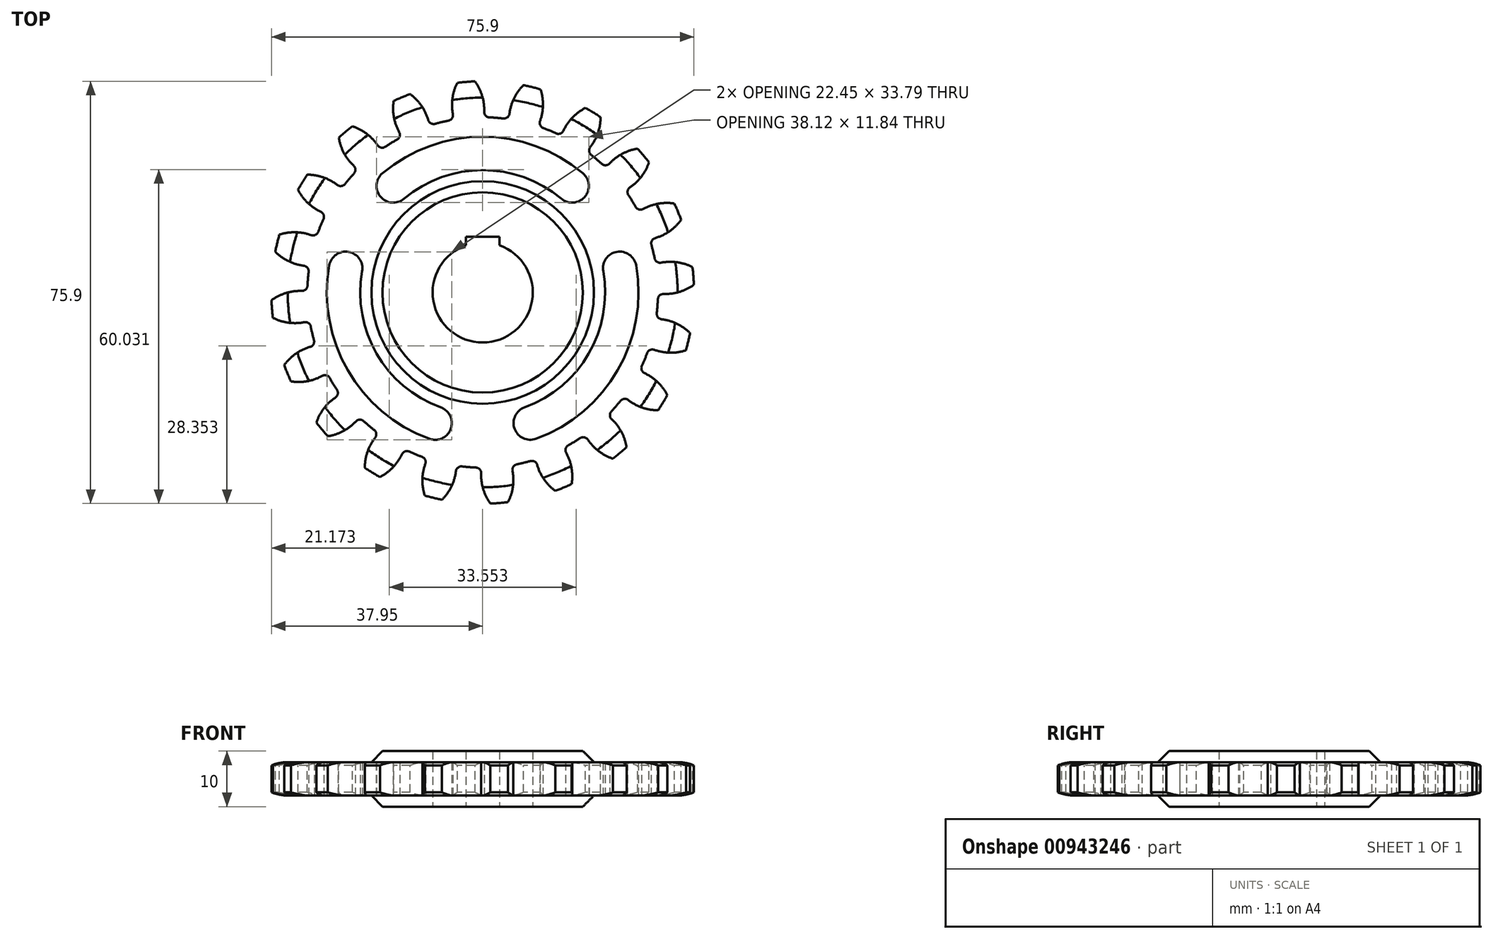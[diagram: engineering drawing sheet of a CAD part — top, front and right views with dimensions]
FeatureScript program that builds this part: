
annotation { "Feature Type Name" : "Feature", "Feature Type Description" : "" }
export const myFeature = defineFeature(function(context is Context, id is Id, definition is map)
    precondition{}
    {
        {
            var Q0;
            Q0=qCreatedBy(makeId("Top.planeOp"),FACE);
            var sketch = newSketch(context, id + "F0", { "sketchPlane" : qUnion([Q0])});
            skArc(sketch, "E0", {"start": v(-3, 8.49) * mm, "mid": v(0, -9) * mm, "end": v(3, 8.49) * mm});
            skCircle(sketch, "E1", {"center": v(0, 0) * mm, "radius": 25 * mm, "construction": true});
            skPoint(sketch, "E2", {"position": v(-46.68, 29.9) * mm});
            skArc(sketch, "E3", {"start": v(-21.67, 3.82) * mm, "mid": v(-24.1, 7.3) * mm, "end": v(-27.57, 4.86) * mm});
            skLineSegment(sketch, "E4", {"start": v(0, 0) * mm, "end": v(-24.62, 4.34) * mm, "construction": true});
            skArc(sketch, "E5", {"start": v(-9.58, -26.31) * mm, "mid": v(-5.73, -24.52) * mm, "end": v(-7.52, -20.67) * mm});
            skLineSegment(sketch, "E6", {"start": v(-8.55, -23.5) * mm, "end": v(0, 0) * mm, "construction": true});
            skArc(sketch, "E7", {"start": v(-27.57, 4.86) * mm, "mid": v(-24.25, -14) * mm, "end": v(-9.58, -26.31) * mm});
            skArc(sketch, "E8", {"start": v(-21.67, 3.82) * mm, "mid": v(-19.05, -11) * mm, "end": v(-7.52, -20.67) * mm});
            skArc(sketch, "E9.1.0", {"start": v(7.52, -20.67) * mm, "mid": v(19.05, -11) * mm, "end": v(21.67, 3.82) * mm});
            skArc(sketch, "E9.1.1", {"start": v(7.52, -20.67) * mm, "mid": v(5.73, -24.52) * mm, "end": v(9.58, -26.31) * mm});
            skArc(sketch, "E9.1.2", {"start": v(9.58, -26.31) * mm, "mid": v(24.25, -14) * mm, "end": v(27.57, 4.86) * mm});
            skArc(sketch, "E9.1.3", {"start": v(27.57, 4.86) * mm, "mid": v(24.1, 7.3) * mm, "end": v(21.67, 3.82) * mm});
            skArc(sketch, "E9.2.0", {"start": v(14.14, 16.85) * mm, "mid": v(0, 22) * mm, "end": v(-14.14, 16.85) * mm});
            skArc(sketch, "E9.2.1", {"start": v(14.14, 16.85) * mm, "mid": v(18.37, 17.22) * mm, "end": v(18, 21.45) * mm});
            skArc(sketch, "E9.2.2", {"start": v(18, 21.45) * mm, "mid": v(0, 28) * mm, "end": v(-18, 21.45) * mm});
            skLineSegment(sketch, "E10", {"start": v(-3, 8.49) * mm, "end": v(-3, 10) * mm});
            skLineSegment(sketch, "E11", {"start": v(-3, 10) * mm, "end": v(3, 10) * mm});
            skLineSegment(sketch, "E12", {"start": v(3, 10) * mm, "end": v(3, 8.49) * mm});
            skArc(sketch, "E13", {"start": v(-18, 21.45) * mm, "mid": v(-18.37, 17.22) * mm, "end": v(-14.14, 16.85) * mm});
            skArc(sketch, "E14", {"start": v(-1.4, 37.97) * mm, "mid": v(-2.98, 37.88) * mm, "end": v(-4.55, 37.73) * mm});
            skArc(sketch, "E15", {"start": v(-28.6, 13.2) * mm, "mid": v(-29.1, 12.05) * mm, "end": v(-29.55, 10.9) * mm});
            skLineSegment(sketch, "E16", {"start": v(0, 0) * mm, "end": v(0, 47.52) * mm, "construction": true});
            skArc(sketch, "E17", {"start": v(0.27, 32.5) * mm, "mid": v(-0.1, 35.38) * mm, "end": v(-1.4, 37.97) * mm});
            skLineSegment(sketch, "E18", {"start": v(0, 0) * mm, "end": v(-2.98, 37.88) * mm, "construction": true});
            skArc(sketch, "E19.MirrorCS", {"start": v(-5.36, 32.07) * mm, "mid": v(-5.43, 34.96) * mm, "end": v(-4.55, 37.73) * mm});
            skArc(sketch, "E20", {"start": v(-5.48, 34.57) * mm, "mid": v(2.75, -34.9) * mm, "end": v(0, 35) * mm, "construction": true});
            skArc(sketch, "E21", {"start": v(0, 35) * mm, "mid": v(-2.75, 34.9) * mm, "end": v(-5.48, 34.57) * mm, "construction": true});
            skArc(sketch, "E22", {"start": v(-6.14, 30.9) * mm, "mid": v(-5.5, 31.32) * mm, "end": v(-5.36, 32.07) * mm});
            skPoint(sketch, "E23.orphan", {"position": v(-5.1, 31.08) * mm});
            skArc(sketch, "E24.MirrorCS", {"start": v(1.23, 31.48) * mm, "mid": v(0.54, 31.8) * mm, "end": v(0.27, 32.5) * mm});
            skPoint(sketch, "E25.orphan", {"position": v(0.18, 31.5) * mm});
            skArc(sketch, "E26.1.0", {"start": v(3.7, 31.28) * mm, "mid": v(4.44, 31.49) * mm, "end": v(4.82, 32.15) * mm});
            skArc(sketch, "E26.1.1", {"start": v(4.82, 32.15) * mm, "mid": v(5.64, 34.93) * mm, "end": v(7.33, 37.29) * mm});
            skArc(sketch, "E26.1.2", {"start": v(10.4, 36.55) * mm, "mid": v(8.87, 36.95) * mm, "end": v(7.33, 37.29) * mm});
            skArc(sketch, "E26.1.3", {"start": v(10.3, 30.83) * mm, "mid": v(10.83, 33.68) * mm, "end": v(10.4, 36.55) * mm});
            skArc(sketch, "E26.1.4", {"start": v(10.9, 29.55) * mm, "mid": v(10.34, 30.07) * mm, "end": v(10.3, 30.83) * mm});
            skArc(sketch, "E26.2.0", {"start": v(13.2, 28.6) * mm, "mid": v(13.95, 28.57) * mm, "end": v(14.51, 29.1) * mm});
            skArc(sketch, "E26.2.1", {"start": v(14.51, 29.1) * mm, "mid": v(16.16, 31.48) * mm, "end": v(18.5, 33.2) * mm});
            skArc(sketch, "E26.2.2", {"start": v(21.18, 31.55) * mm, "mid": v(19.86, 32.4) * mm, "end": v(18.5, 33.2) * mm});
            skArc(sketch, "E26.2.3", {"start": v(19.33, 26.14) * mm, "mid": v(20.7, 28.69) * mm, "end": v(21.18, 31.55) * mm});
            skArc(sketch, "E26.2.4", {"start": v(19.5, 24.74) * mm, "mid": v(19.13, 25.4) * mm, "end": v(19.33, 26.14) * mm});
            skArc(sketch, "E26.3.0", {"start": v(21.38, 23.13) * mm, "mid": v(22.1, 22.86) * mm, "end": v(22.8, 23.18) * mm});
            skArc(sketch, "E26.3.1", {"start": v(22.8, 23.18) * mm, "mid": v(25.1, 24.94) * mm, "end": v(27.85, 25.86) * mm});
            skArc(sketch, "E26.3.2", {"start": v(29.9, 23.46) * mm, "mid": v(28.9, 24.68) * mm, "end": v(27.85, 25.86) * mm});
            skArc(sketch, "E26.3.3", {"start": v(26.46, 18.89) * mm, "mid": v(28.56, 20.89) * mm, "end": v(29.9, 23.46) * mm});
            skArc(sketch, "E26.3.4", {"start": v(26.19, 17.5) * mm, "mid": v(26.04, 18.25) * mm, "end": v(26.46, 18.89) * mm});
            skArc(sketch, "E26.4.0", {"start": v(27.48, 15.39) * mm, "mid": v(28.08, 14.92) * mm, "end": v(28.84, 15) * mm});
            skArc(sketch, "E26.4.1", {"start": v(28.84, 15) * mm, "mid": v(31.58, 15.97) * mm, "end": v(34.47, 15.98) * mm});
            skArc(sketch, "E26.4.2", {"start": v(35.68, 13.07) * mm, "mid": v(35.1, 14.54) * mm, "end": v(34.47, 15.98) * mm});
            skArc(sketch, "E26.4.3", {"start": v(31, 9.79) * mm, "mid": v(33.62, 11.04) * mm, "end": v(35.68, 13.07) * mm});
            skArc(sketch, "E26.4.4", {"start": v(30.32, 8.55) * mm, "mid": v(30.4, 9.31) * mm, "end": v(31, 9.79) * mm});
            skArc(sketch, "E26.5.0", {"start": v(30.9, 6.14) * mm, "mid": v(31.32, 5.5) * mm, "end": v(32.07, 5.36) * mm});
            skArc(sketch, "E26.5.1", {"start": v(32.07, 5.36) * mm, "mid": v(34.96, 5.43) * mm, "end": v(37.73, 4.55) * mm});
            skArc(sketch, "E26.5.2", {"start": v(37.97, 1.4) * mm, "mid": v(37.88, 2.98) * mm, "end": v(37.73, 4.55) * mm});
            skArc(sketch, "E26.5.3", {"start": v(32.5, -0.27) * mm, "mid": v(35.38, 0.1) * mm, "end": v(37.97, 1.4) * mm});
            skArc(sketch, "E26.5.4", {"start": v(31.48, -1.23) * mm, "mid": v(31.8, -0.54) * mm, "end": v(32.5, -0.27) * mm});
            skArc(sketch, "E26.6.0", {"start": v(31.28, -3.7) * mm, "mid": v(31.49, -4.44) * mm, "end": v(32.15, -4.82) * mm});
            skArc(sketch, "E26.6.1", {"start": v(32.15, -4.82) * mm, "mid": v(34.93, -5.64) * mm, "end": v(37.29, -7.33) * mm});
            skArc(sketch, "E26.6.2", {"start": v(36.55, -10.4) * mm, "mid": v(36.95, -8.87) * mm, "end": v(37.29, -7.33) * mm});
            skArc(sketch, "E26.6.3", {"start": v(30.83, -10.3) * mm, "mid": v(33.68, -10.83) * mm, "end": v(36.55, -10.4) * mm});
            skArc(sketch, "E26.6.4", {"start": v(29.55, -10.9) * mm, "mid": v(30.07, -10.34) * mm, "end": v(30.83, -10.3) * mm});
            skArc(sketch, "E26.7.0", {"start": v(28.6, -13.2) * mm, "mid": v(28.57, -13.95) * mm, "end": v(29.1, -14.51) * mm});
            skArc(sketch, "E26.7.1", {"start": v(29.1, -14.51) * mm, "mid": v(31.48, -16.16) * mm, "end": v(33.2, -18.5) * mm});
            skArc(sketch, "E26.7.2", {"start": v(31.55, -21.18) * mm, "mid": v(32.4, -19.86) * mm, "end": v(33.2, -18.5) * mm});
            skArc(sketch, "E26.7.3", {"start": v(26.14, -19.33) * mm, "mid": v(28.69, -20.7) * mm, "end": v(31.55, -21.18) * mm});
            skArc(sketch, "E26.7.4", {"start": v(24.74, -19.5) * mm, "mid": v(25.4, -19.13) * mm, "end": v(26.14, -19.33) * mm});
            skArc(sketch, "E26.8.0", {"start": v(23.13, -21.38) * mm, "mid": v(22.86, -22.1) * mm, "end": v(23.18, -22.8) * mm});
            skArc(sketch, "E26.8.1", {"start": v(23.18, -22.8) * mm, "mid": v(24.94, -25.1) * mm, "end": v(25.86, -27.85) * mm});
            skArc(sketch, "E26.8.2", {"start": v(23.46, -29.9) * mm, "mid": v(24.68, -28.9) * mm, "end": v(25.86, -27.85) * mm});
            skArc(sketch, "E26.8.3", {"start": v(18.89, -26.46) * mm, "mid": v(20.89, -28.56) * mm, "end": v(23.46, -29.9) * mm});
            skArc(sketch, "E26.8.4", {"start": v(17.5, -26.19) * mm, "mid": v(18.25, -26.04) * mm, "end": v(18.89, -26.46) * mm});
            skArc(sketch, "E26.9.0", {"start": v(15.39, -27.48) * mm, "mid": v(14.92, -28.08) * mm, "end": v(15, -28.84) * mm});
            skArc(sketch, "E26.9.1", {"start": v(15, -28.84) * mm, "mid": v(15.97, -31.58) * mm, "end": v(15.98, -34.47) * mm});
            skArc(sketch, "E26.9.2", {"start": v(13.07, -35.68) * mm, "mid": v(14.54, -35.1) * mm, "end": v(15.98, -34.47) * mm});
            skArc(sketch, "E26.9.3", {"start": v(9.79, -31) * mm, "mid": v(11.04, -33.62) * mm, "end": v(13.07, -35.68) * mm});
            skArc(sketch, "E26.9.4", {"start": v(8.55, -30.32) * mm, "mid": v(9.31, -30.4) * mm, "end": v(9.79, -31) * mm});
            skArc(sketch, "E26.10.0", {"start": v(6.14, -30.9) * mm, "mid": v(5.5, -31.32) * mm, "end": v(5.36, -32.07) * mm});
            skArc(sketch, "E26.10.1", {"start": v(5.36, -32.07) * mm, "mid": v(5.43, -34.96) * mm, "end": v(4.55, -37.73) * mm});
            skArc(sketch, "E26.10.2", {"start": v(1.4, -37.97) * mm, "mid": v(2.98, -37.88) * mm, "end": v(4.55, -37.73) * mm});
            skArc(sketch, "E26.10.3", {"start": v(-0.27, -32.5) * mm, "mid": v(0.1, -35.38) * mm, "end": v(1.4, -37.97) * mm});
            skArc(sketch, "E26.10.4", {"start": v(-1.23, -31.48) * mm, "mid": v(-0.54, -31.8) * mm, "end": v(-0.27, -32.5) * mm});
            skArc(sketch, "E26.11.0", {"start": v(-3.7, -31.28) * mm, "mid": v(-4.44, -31.49) * mm, "end": v(-4.82, -32.15) * mm});
            skArc(sketch, "E26.11.1", {"start": v(-4.82, -32.15) * mm, "mid": v(-5.64, -34.93) * mm, "end": v(-7.33, -37.29) * mm});
            skArc(sketch, "E26.11.2", {"start": v(-10.4, -36.55) * mm, "mid": v(-8.87, -36.95) * mm, "end": v(-7.33, -37.29) * mm});
            skArc(sketch, "E26.11.3", {"start": v(-10.3, -30.83) * mm, "mid": v(-10.83, -33.68) * mm, "end": v(-10.4, -36.55) * mm});
            skArc(sketch, "E26.11.4", {"start": v(-10.9, -29.55) * mm, "mid": v(-10.34, -30.07) * mm, "end": v(-10.3, -30.83) * mm});
            skArc(sketch, "E26.12.0", {"start": v(-13.2, -28.6) * mm, "mid": v(-13.95, -28.57) * mm, "end": v(-14.51, -29.1) * mm});
            skArc(sketch, "E26.12.1", {"start": v(-14.51, -29.1) * mm, "mid": v(-16.16, -31.48) * mm, "end": v(-18.5, -33.2) * mm});
            skArc(sketch, "E26.12.2", {"start": v(-21.18, -31.55) * mm, "mid": v(-19.86, -32.4) * mm, "end": v(-18.5, -33.2) * mm});
            skArc(sketch, "E26.12.3", {"start": v(-19.33, -26.14) * mm, "mid": v(-20.7, -28.69) * mm, "end": v(-21.18, -31.55) * mm});
            skArc(sketch, "E26.12.4", {"start": v(-19.5, -24.74) * mm, "mid": v(-19.13, -25.4) * mm, "end": v(-19.33, -26.14) * mm});
            skArc(sketch, "E26.13.0", {"start": v(-21.38, -23.13) * mm, "mid": v(-22.1, -22.86) * mm, "end": v(-22.8, -23.18) * mm});
            skArc(sketch, "E26.13.1", {"start": v(-22.8, -23.18) * mm, "mid": v(-25.1, -24.94) * mm, "end": v(-27.85, -25.86) * mm});
            skArc(sketch, "E26.13.2", {"start": v(-29.9, -23.46) * mm, "mid": v(-28.9, -24.68) * mm, "end": v(-27.85, -25.86) * mm});
            skArc(sketch, "E26.13.3", {"start": v(-26.46, -18.89) * mm, "mid": v(-28.56, -20.89) * mm, "end": v(-29.9, -23.46) * mm});
            skArc(sketch, "E26.13.4", {"start": v(-26.19, -17.5) * mm, "mid": v(-26.04, -18.25) * mm, "end": v(-26.46, -18.89) * mm});
            skArc(sketch, "E26.14.0", {"start": v(-27.48, -15.39) * mm, "mid": v(-28.08, -14.92) * mm, "end": v(-28.84, -15) * mm});
            skArc(sketch, "E26.14.1", {"start": v(-28.84, -15) * mm, "mid": v(-31.58, -15.97) * mm, "end": v(-34.47, -15.98) * mm});
            skArc(sketch, "E26.14.2", {"start": v(-35.68, -13.07) * mm, "mid": v(-35.1, -14.54) * mm, "end": v(-34.47, -15.98) * mm});
            skArc(sketch, "E26.14.3", {"start": v(-31, -9.79) * mm, "mid": v(-33.62, -11.04) * mm, "end": v(-35.68, -13.07) * mm});
            skArc(sketch, "E26.14.4", {"start": v(-30.32, -8.55) * mm, "mid": v(-30.4, -9.31) * mm, "end": v(-31, -9.79) * mm});
            skArc(sketch, "E26.15.0", {"start": v(-30.9, -6.14) * mm, "mid": v(-31.32, -5.5) * mm, "end": v(-32.07, -5.36) * mm});
            skArc(sketch, "E26.15.1", {"start": v(-32.07, -5.36) * mm, "mid": v(-34.96, -5.43) * mm, "end": v(-37.73, -4.55) * mm});
            skArc(sketch, "E26.15.2", {"start": v(-37.97, -1.4) * mm, "mid": v(-37.88, -2.98) * mm, "end": v(-37.73, -4.55) * mm});
            skArc(sketch, "E26.15.3", {"start": v(-32.5, 0.27) * mm, "mid": v(-35.38, -0.1) * mm, "end": v(-37.97, -1.4) * mm});
            skArc(sketch, "E26.15.4", {"start": v(-31.48, 1.23) * mm, "mid": v(-31.8, 0.54) * mm, "end": v(-32.5, 0.27) * mm});
            skArc(sketch, "E26.16.0", {"start": v(-31.28, 3.7) * mm, "mid": v(-31.49, 4.44) * mm, "end": v(-32.15, 4.82) * mm});
            skArc(sketch, "E26.16.1", {"start": v(-32.15, 4.82) * mm, "mid": v(-34.93, 5.64) * mm, "end": v(-37.29, 7.33) * mm});
            skArc(sketch, "E26.16.2", {"start": v(-36.55, 10.4) * mm, "mid": v(-36.95, 8.87) * mm, "end": v(-37.29, 7.33) * mm});
            skArc(sketch, "E26.16.3", {"start": v(-30.83, 10.3) * mm, "mid": v(-33.68, 10.83) * mm, "end": v(-36.55, 10.4) * mm});
            skArc(sketch, "E26.16.4", {"start": v(-29.55, 10.9) * mm, "mid": v(-30.07, 10.34) * mm, "end": v(-30.83, 10.3) * mm});
            skArc(sketch, "E26.17.0", {"start": v(-28.6, 13.2) * mm, "mid": v(-28.57, 13.95) * mm, "end": v(-29.1, 14.51) * mm});
            skArc(sketch, "E26.17.1", {"start": v(-29.1, 14.51) * mm, "mid": v(-31.48, 16.16) * mm, "end": v(-33.2, 18.5) * mm});
            skArc(sketch, "E26.17.2", {"start": v(-31.55, 21.18) * mm, "mid": v(-32.4, 19.86) * mm, "end": v(-33.2, 18.5) * mm});
            skArc(sketch, "E26.17.3", {"start": v(-26.14, 19.33) * mm, "mid": v(-28.69, 20.7) * mm, "end": v(-31.55, 21.18) * mm});
            skArc(sketch, "E26.17.4", {"start": v(-24.74, 19.5) * mm, "mid": v(-25.4, 19.13) * mm, "end": v(-26.14, 19.33) * mm});
            skArc(sketch, "E26.18.0", {"start": v(-23.13, 21.38) * mm, "mid": v(-22.86, 22.1) * mm, "end": v(-23.18, 22.8) * mm});
            skArc(sketch, "E26.18.1", {"start": v(-23.18, 22.8) * mm, "mid": v(-24.94, 25.1) * mm, "end": v(-25.86, 27.85) * mm});
            skArc(sketch, "E26.18.2", {"start": v(-23.46, 29.9) * mm, "mid": v(-24.68, 28.9) * mm, "end": v(-25.86, 27.85) * mm});
            skArc(sketch, "E26.18.3", {"start": v(-18.89, 26.46) * mm, "mid": v(-20.89, 28.56) * mm, "end": v(-23.46, 29.9) * mm});
            skArc(sketch, "E26.18.4", {"start": v(-17.5, 26.19) * mm, "mid": v(-18.25, 26.04) * mm, "end": v(-18.89, 26.46) * mm});
            skArc(sketch, "E26.19.0", {"start": v(-15.39, 27.48) * mm, "mid": v(-14.92, 28.08) * mm, "end": v(-15, 28.84) * mm});
            skArc(sketch, "E26.19.1", {"start": v(-15, 28.84) * mm, "mid": v(-15.97, 31.58) * mm, "end": v(-15.98, 34.47) * mm});
            skArc(sketch, "E26.19.2", {"start": v(-13.07, 35.68) * mm, "mid": v(-14.54, 35.1) * mm, "end": v(-15.98, 34.47) * mm});
            skArc(sketch, "E26.19.3", {"start": v(-9.79, 31) * mm, "mid": v(-11.04, 33.62) * mm, "end": v(-13.07, 35.68) * mm});
            skArc(sketch, "E26.19.4", {"start": v(-8.55, 30.32) * mm, "mid": v(-9.31, 30.4) * mm, "end": v(-9.79, 31) * mm});
            skLineSegment(sketch, "E26.anchor1", {"start": v(0, 0) * mm, "end": v(-6.14, 30.9) * mm, "construction": true});
            skLineSegment(sketch, "E26.anchor2", {"start": v(0, 0) * mm, "end": v(-15.39, 27.48) * mm, "construction": true});
            skArc(sketch, "E27.trimOffspring", {"start": v(-23.13, 21.38) * mm, "mid": v(-23.95, 20.46) * mm, "end": v(-24.74, 19.5) * mm});
            skArc(sketch, "E28.trimOffspring", {"start": v(-15.39, 27.48) * mm, "mid": v(-16.46, 26.86) * mm, "end": v(-17.5, 26.19) * mm});
            skArc(sketch, "E29.trimOffspring", {"start": v(-6.14, 30.9) * mm, "mid": v(-7.35, 30.63) * mm, "end": v(-8.55, 30.32) * mm});
            skArc(sketch, "E30.trimOffspring", {"start": v(3.7, 31.28) * mm, "mid": v(2.47, 31.4) * mm, "end": v(1.23, 31.48) * mm});
            skArc(sketch, "E31.trimOffspring", {"start": v(13.2, 28.6) * mm, "mid": v(12.05, 29.1) * mm, "end": v(10.9, 29.55) * mm});
            skArc(sketch, "E32.trimOffspring", {"start": v(21.38, 23.13) * mm, "mid": v(20.46, 23.95) * mm, "end": v(19.5, 24.74) * mm});
            skArc(sketch, "E33.trimOffspring", {"start": v(27.48, 15.39) * mm, "mid": v(26.86, 16.46) * mm, "end": v(26.19, 17.5) * mm});
            skArc(sketch, "E34.trimOffspring", {"start": v(30.9, 6.14) * mm, "mid": v(30.63, 7.35) * mm, "end": v(30.32, 8.55) * mm});
            skArc(sketch, "E35.trimOffspring", {"start": v(31.28, -3.7) * mm, "mid": v(31.4, -2.47) * mm, "end": v(31.48, -1.23) * mm});
            skArc(sketch, "E36.trimOffspring", {"start": v(28.6, -13.2) * mm, "mid": v(29.1, -12.05) * mm, "end": v(29.55, -10.9) * mm});
            skArc(sketch, "E37.trimOffspring", {"start": v(23.13, -21.38) * mm, "mid": v(23.95, -20.46) * mm, "end": v(24.74, -19.5) * mm});
            skArc(sketch, "E38.trimOffspring", {"start": v(15.39, -27.48) * mm, "mid": v(16.46, -26.86) * mm, "end": v(17.5, -26.19) * mm});
            skArc(sketch, "E39.trimOffspring", {"start": v(6.14, -30.9) * mm, "mid": v(7.35, -30.63) * mm, "end": v(8.55, -30.32) * mm});
            skArc(sketch, "E40.trimOffspring", {"start": v(-3.7, -31.28) * mm, "mid": v(-2.47, -31.4) * mm, "end": v(-1.23, -31.48) * mm});
            skArc(sketch, "E41.trimOffspring", {"start": v(-13.2, -28.6) * mm, "mid": v(-12.05, -29.1) * mm, "end": v(-10.9, -29.55) * mm});
            skArc(sketch, "E42.trimOffspring", {"start": v(-21.38, -23.13) * mm, "mid": v(-20.46, -23.95) * mm, "end": v(-19.5, -24.74) * mm});
            skArc(sketch, "E43.trimOffspring", {"start": v(-27.48, -15.39) * mm, "mid": v(-26.86, -16.46) * mm, "end": v(-26.19, -17.5) * mm});
            skArc(sketch, "E44.trimOffspring", {"start": v(-30.9, -6.14) * mm, "mid": v(-30.63, -7.35) * mm, "end": v(-30.32, -8.55) * mm});
            skArc(sketch, "E45.trimOffspring", {"start": v(-31.28, 3.7) * mm, "mid": v(-31.4, 2.47) * mm, "end": v(-31.48, 1.23) * mm});
            skSolve(sketch);
        }
        {
            var Q0;
            Q0=makeQuery(id+"F0.imprint","IMPRINT",FACE,{"disambiguationData":[TD([[makeQuery(id+"F0.imprint","IMPRINT",EDGE,{"derivedFrom":sQuery(id+"F0.wireOp",EDGE,"E0")}),-1.0]])]});
            extrude(context, id + "F1", {"entities" : qUnion([Q0]), "endBound" : BoundingType.SYMMETRIC, "depth" : 6 * mm, "offsetDistance" : 25 * mm});
        }
        {
            var Q0;
            Q0=qCreatedBy(makeId("Right.planeOp"),FACE);
            var sketch = newSketch(context, id + "F2", { "sketchPlane" : qUnion([Q0])});
            skLineSegment(sketch, "E46", {"start": v(37.97, 2.44) * mm, "end": v(37.97, -2.43) * mm});
            skLineSegment(sketch, "E47", {"start": v(34.73, 3) * mm, "end": v(34.73, -9.64) * mm, "construction": true});
            skArc(sketch, "E48", {"start": v(37.97, 2.44) * mm, "mid": v(36.38, 2.87) * mm, "end": v(34.73, 3) * mm});
            skArc(sketch, "E49.MirrorCS", {"start": v(37.97, -2.44) * mm, "mid": v(36.38, -2.87) * mm, "end": v(34.73, -3) * mm});
            skLineSegment(sketch, "E50", {"start": v(34.73, 3) * mm, "end": v(34.73, 3.33) * mm});
            skLineSegment(sketch, "E51", {"start": v(34.73, 3.33) * mm, "end": v(39.08, 3.33) * mm});
            skLineSegment(sketch, "E52", {"start": v(39.08, 3.33) * mm, "end": v(39.08, -3.22) * mm});
            skLineSegment(sketch, "E53", {"start": v(39.08, -3.22) * mm, "end": v(34.73, -3.32) * mm});
            skLineSegment(sketch, "E54", {"start": v(34.73, -3.32) * mm, "end": v(34.73, -3) * mm});
            skSolve(sketch);
        }
        {
            var Q0;
            Q0=makeQuery(id+"F2.imprint","IMPRINT",FACE,{"disambiguationData":[TD([[makeQuery(id+"F2.imprint","IMPRINT",EDGE,{"derivedFrom":sQuery(id+"F2.wireOp",EDGE,"E46")}),1.0]])]});
            var Q1;
            Q1=makeQuery(id+"F1.opExtrude","SWEPT_FACE",FACE,{"disambiguationData":[OSD([sQuery(id+"F0.wireOp",EDGE,"E0")])]});
            revolve(context, id + "F3", {"operationType" : NewBodyOperationType.REMOVE, "surfaceOperationType" : NewSurfaceOperationType.NEW, "entities" : qUnion([Q0]), "axis" : qUnion([Q1]), "revolveType" : RevolveType.FULL, "oppositeDirection" : true});
        }
        {
            var Q0;
            Q0=qCreatedBy(makeId("Top.planeOp"),FACE);
            var sketch = newSketch(context, id + "F4", { "sketchPlane" : qUnion([Q0])});
            skCircle(sketch, "E55", {"center": v(0, 0) * mm, "radius": 18 * mm});
            skArc(sketch, "E56", {"start": v(-3, 8.49) * mm, "mid": v(0, -9) * mm, "end": v(3, 8.49) * mm});
            skLineSegment(sketch, "E57", {"start": v(3, 8.49) * mm, "end": v(3, 10) * mm});
            skLineSegment(sketch, "E58", {"start": v(3, 10) * mm, "end": v(-3, 10) * mm});
            skLineSegment(sketch, "E59", {"start": v(-3, 10) * mm, "end": v(-3, 8.49) * mm});
            skSolve(sketch);
        }
        {
            var Q0;
            Q0=qSketchRegion(id+"F4",true);
            extrude(context, id + "F5", {"entities" : qUnion([Q0]), "operationType" : NewBodyOperationType.ADD, "endBound" : BoundingType.SYMMETRIC, "depth" : 10 * mm, "offsetDistance" : 25 * mm});
        }
        {
            var Q0;
            Q0=makeQuery(id+"F5.boolean.opBoolean","INTERSECT",EDGE,{"derivedFrom":[makeQuery(id+"F1.opExtrude","CAP_FACE",FACE,{"disambiguationData":[OSD([sQuery(id+"F0.wireOp",EDGE,"E0"),sQuery(id+"F0.wireOp",EDGE,"E3"),sQuery(id+"F0.wireOp",EDGE,"E5"),sQuery(id+"F0.wireOp",EDGE,"E7"),sQuery(id+"F0.wireOp",EDGE,"E8"),sQuery(id+"F0.wireOp",EDGE,"E9.1.0"),sQuery(id+"F0.wireOp",EDGE,"E9.1.1"),sQuery(id+"F0.wireOp",EDGE,"E9.1.2"),sQuery(id+"F0.wireOp",EDGE,"E9.1.3"),sQuery(id+"F0.wireOp",EDGE,"E9.2.0"),sQuery(id+"F0.wireOp",EDGE,"E9.2.1"),sQuery(id+"F0.wireOp",EDGE,"E9.2.2"),sQuery(id+"F0.wireOp",EDGE,"E10"),sQuery(id+"F0.wireOp",EDGE,"E11"),sQuery(id+"F0.wireOp",EDGE,"E12"),sQuery(id+"F0.wireOp",EDGE,"E13"),sQuery(id+"F0.wireOp",EDGE,"E14"),sQuery(id+"F0.wireOp",EDGE,"E15"),sQuery(id+"F0.wireOp",EDGE,"E17"),sQuery(id+"F0.wireOp",EDGE,"E19.MirrorCS"),sQuery(id+"F0.wireOp",EDGE,"E22"),sQuery(id+"F0.wireOp",EDGE,"E24.MirrorCS"),sQuery(id+"F0.wireOp",EDGE,"E26.1.0"),sQuery(id+"F0.wireOp",EDGE,"E26.1.1"),sQuery(id+"F0.wireOp",EDGE,"E26.1.2"),sQuery(id+"F0.wireOp",EDGE,"E26.1.3"),sQuery(id+"F0.wireOp",EDGE,"E26.1.4"),sQuery(id+"F0.wireOp",EDGE,"E26.2.0"),sQuery(id+"F0.wireOp",EDGE,"E26.2.1"),sQuery(id+"F0.wireOp",EDGE,"E26.2.2"),sQuery(id+"F0.wireOp",EDGE,"E26.2.3"),sQuery(id+"F0.wireOp",EDGE,"E26.2.4"),sQuery(id+"F0.wireOp",EDGE,"E26.3.0"),sQuery(id+"F0.wireOp",EDGE,"E26.3.1"),sQuery(id+"F0.wireOp",EDGE,"E26.3.2"),sQuery(id+"F0.wireOp",EDGE,"E26.3.3"),sQuery(id+"F0.wireOp",EDGE,"E26.3.4"),sQuery(id+"F0.wireOp",EDGE,"E26.4.0"),sQuery(id+"F0.wireOp",EDGE,"E26.4.1"),sQuery(id+"F0.wireOp",EDGE,"E26.4.2"),sQuery(id+"F0.wireOp",EDGE,"E26.4.3"),sQuery(id+"F0.wireOp",EDGE,"E26.4.4"),sQuery(id+"F0.wireOp",EDGE,"E26.5.0"),sQuery(id+"F0.wireOp",EDGE,"E26.5.1"),sQuery(id+"F0.wireOp",EDGE,"E26.5.2"),sQuery(id+"F0.wireOp",EDGE,"E26.5.3"),sQuery(id+"F0.wireOp",EDGE,"E26.5.4"),sQuery(id+"F0.wireOp",EDGE,"E26.6.0"),sQuery(id+"F0.wireOp",EDGE,"E26.6.1"),sQuery(id+"F0.wireOp",EDGE,"E26.6.2"),sQuery(id+"F0.wireOp",EDGE,"E26.6.3"),sQuery(id+"F0.wireOp",EDGE,"E26.6.4"),sQuery(id+"F0.wireOp",EDGE,"E26.7.0"),sQuery(id+"F0.wireOp",EDGE,"E26.7.1"),sQuery(id+"F0.wireOp",EDGE,"E26.7.2"),sQuery(id+"F0.wireOp",EDGE,"E26.7.3"),sQuery(id+"F0.wireOp",EDGE,"E26.7.4"),sQuery(id+"F0.wireOp",EDGE,"E26.8.0"),sQuery(id+"F0.wireOp",EDGE,"E26.8.1"),sQuery(id+"F0.wireOp",EDGE,"E26.8.2"),sQuery(id+"F0.wireOp",EDGE,"E26.8.3"),sQuery(id+"F0.wireOp",EDGE,"E26.8.4"),sQuery(id+"F0.wireOp",EDGE,"E26.9.0"),sQuery(id+"F0.wireOp",EDGE,"E26.9.1"),sQuery(id+"F0.wireOp",EDGE,"E26.9.2"),sQuery(id+"F0.wireOp",EDGE,"E26.9.3"),sQuery(id+"F0.wireOp",EDGE,"E26.9.4"),sQuery(id+"F0.wireOp",EDGE,"E26.10.0"),sQuery(id+"F0.wireOp",EDGE,"E26.10.1"),sQuery(id+"F0.wireOp",EDGE,"E26.10.2"),sQuery(id+"F0.wireOp",EDGE,"E26.10.3"),sQuery(id+"F0.wireOp",EDGE,"E26.10.4"),sQuery(id+"F0.wireOp",EDGE,"E26.11.0"),sQuery(id+"F0.wireOp",EDGE,"E26.11.1"),sQuery(id+"F0.wireOp",EDGE,"E26.11.2"),sQuery(id+"F0.wireOp",EDGE,"E26.11.3"),sQuery(id+"F0.wireOp",EDGE,"E26.11.4"),sQuery(id+"F0.wireOp",EDGE,"E26.12.0"),sQuery(id+"F0.wireOp",EDGE,"E26.12.1"),sQuery(id+"F0.wireOp",EDGE,"E26.12.2"),sQuery(id+"F0.wireOp",EDGE,"E26.12.3"),sQuery(id+"F0.wireOp",EDGE,"E26.12.4"),sQuery(id+"F0.wireOp",EDGE,"E26.13.0"),sQuery(id+"F0.wireOp",EDGE,"E26.13.1"),sQuery(id+"F0.wireOp",EDGE,"E26.13.2"),sQuery(id+"F0.wireOp",EDGE,"E26.13.3"),sQuery(id+"F0.wireOp",EDGE,"E26.13.4"),sQuery(id+"F0.wireOp",EDGE,"E26.14.0"),sQuery(id+"F0.wireOp",EDGE,"E26.14.1"),sQuery(id+"F0.wireOp",EDGE,"E26.14.2"),sQuery(id+"F0.wireOp",EDGE,"E26.14.3"),sQuery(id+"F0.wireOp",EDGE,"E26.14.4"),sQuery(id+"F0.wireOp",EDGE,"E26.15.0"),sQuery(id+"F0.wireOp",EDGE,"E26.15.1"),sQuery(id+"F0.wireOp",EDGE,"E26.15.2"),sQuery(id+"F0.wireOp",EDGE,"E26.15.3"),sQuery(id+"F0.wireOp",EDGE,"E26.15.4"),sQuery(id+"F0.wireOp",EDGE,"E26.16.0"),sQuery(id+"F0.wireOp",EDGE,"E26.16.1"),sQuery(id+"F0.wireOp",EDGE,"E26.16.2"),sQuery(id+"F0.wireOp",EDGE,"E26.16.3"),sQuery(id+"F0.wireOp",EDGE,"E26.16.4"),sQuery(id+"F0.wireOp",EDGE,"E26.17.0"),sQuery(id+"F0.wireOp",EDGE,"E26.17.1"),sQuery(id+"F0.wireOp",EDGE,"E26.17.2"),sQuery(id+"F0.wireOp",EDGE,"E26.17.3"),sQuery(id+"F0.wireOp",EDGE,"E26.17.4"),sQuery(id+"F0.wireOp",EDGE,"E26.18.0"),sQuery(id+"F0.wireOp",EDGE,"E26.18.1"),sQuery(id+"F0.wireOp",EDGE,"E26.18.2"),sQuery(id+"F0.wireOp",EDGE,"E26.18.3"),sQuery(id+"F0.wireOp",EDGE,"E26.18.4"),sQuery(id+"F0.wireOp",EDGE,"E26.19.0"),sQuery(id+"F0.wireOp",EDGE,"E26.19.1"),sQuery(id+"F0.wireOp",EDGE,"E26.19.2"),sQuery(id+"F0.wireOp",EDGE,"E26.19.3"),sQuery(id+"F0.wireOp",EDGE,"E26.19.4"),sQuery(id+"F0.wireOp",EDGE,"E27.trimOffspring"),sQuery(id+"F0.wireOp",EDGE,"E28.trimOffspring"),sQuery(id+"F0.wireOp",EDGE,"E29.trimOffspring"),sQuery(id+"F0.wireOp",EDGE,"E30.trimOffspring"),sQuery(id+"F0.wireOp",EDGE,"E31.trimOffspring"),sQuery(id+"F0.wireOp",EDGE,"E32.trimOffspring"),sQuery(id+"F0.wireOp",EDGE,"E33.trimOffspring"),sQuery(id+"F0.wireOp",EDGE,"E34.trimOffspring"),sQuery(id+"F0.wireOp",EDGE,"E35.trimOffspring"),sQuery(id+"F0.wireOp",EDGE,"E36.trimOffspring"),sQuery(id+"F0.wireOp",EDGE,"E37.trimOffspring"),sQuery(id+"F0.wireOp",EDGE,"E38.trimOffspring"),sQuery(id+"F0.wireOp",EDGE,"E39.trimOffspring"),sQuery(id+"F0.wireOp",EDGE,"E40.trimOffspring"),sQuery(id+"F0.wireOp",EDGE,"E41.trimOffspring"),sQuery(id+"F0.wireOp",EDGE,"E42.trimOffspring"),sQuery(id+"F0.wireOp",EDGE,"E43.trimOffspring"),sQuery(id+"F0.wireOp",EDGE,"E44.trimOffspring"),sQuery(id+"F0.wireOp",EDGE,"E45.trimOffspring")])],"isStart":false}),makeQuery(id+"F5.opExtrude","SWEPT_FACE",FACE,{"disambiguationData":[OSD([sQuery(id+"F4.wireOp",EDGE,"E55")])]})]});
            chamfer(context, id + "F6", {"entities" : qUnion([Q0]), "width" : 2 * mm, "tangentPropagation" : true});
        }
        {
            var Q0;
            Q0=makeQuery(id+"F5.boolean.opBoolean","INTERSECT",EDGE,{"derivedFrom":[makeQuery(id+"F1.opExtrude","CAP_FACE",FACE,{"disambiguationData":[OSD([sQuery(id+"F0.wireOp",EDGE,"E0"),sQuery(id+"F0.wireOp",EDGE,"E3"),sQuery(id+"F0.wireOp",EDGE,"E5"),sQuery(id+"F0.wireOp",EDGE,"E7"),sQuery(id+"F0.wireOp",EDGE,"E8"),sQuery(id+"F0.wireOp",EDGE,"E9.1.0"),sQuery(id+"F0.wireOp",EDGE,"E9.1.1"),sQuery(id+"F0.wireOp",EDGE,"E9.1.2"),sQuery(id+"F0.wireOp",EDGE,"E9.1.3"),sQuery(id+"F0.wireOp",EDGE,"E9.2.0"),sQuery(id+"F0.wireOp",EDGE,"E9.2.1"),sQuery(id+"F0.wireOp",EDGE,"E9.2.2"),sQuery(id+"F0.wireOp",EDGE,"E10"),sQuery(id+"F0.wireOp",EDGE,"E11"),sQuery(id+"F0.wireOp",EDGE,"E12"),sQuery(id+"F0.wireOp",EDGE,"E13"),sQuery(id+"F0.wireOp",EDGE,"E14"),sQuery(id+"F0.wireOp",EDGE,"E15"),sQuery(id+"F0.wireOp",EDGE,"E17"),sQuery(id+"F0.wireOp",EDGE,"E19.MirrorCS"),sQuery(id+"F0.wireOp",EDGE,"E22"),sQuery(id+"F0.wireOp",EDGE,"E24.MirrorCS"),sQuery(id+"F0.wireOp",EDGE,"E26.1.0"),sQuery(id+"F0.wireOp",EDGE,"E26.1.1"),sQuery(id+"F0.wireOp",EDGE,"E26.1.2"),sQuery(id+"F0.wireOp",EDGE,"E26.1.3"),sQuery(id+"F0.wireOp",EDGE,"E26.1.4"),sQuery(id+"F0.wireOp",EDGE,"E26.2.0"),sQuery(id+"F0.wireOp",EDGE,"E26.2.1"),sQuery(id+"F0.wireOp",EDGE,"E26.2.2"),sQuery(id+"F0.wireOp",EDGE,"E26.2.3"),sQuery(id+"F0.wireOp",EDGE,"E26.2.4"),sQuery(id+"F0.wireOp",EDGE,"E26.3.0"),sQuery(id+"F0.wireOp",EDGE,"E26.3.1"),sQuery(id+"F0.wireOp",EDGE,"E26.3.2"),sQuery(id+"F0.wireOp",EDGE,"E26.3.3"),sQuery(id+"F0.wireOp",EDGE,"E26.3.4"),sQuery(id+"F0.wireOp",EDGE,"E26.4.0"),sQuery(id+"F0.wireOp",EDGE,"E26.4.1"),sQuery(id+"F0.wireOp",EDGE,"E26.4.2"),sQuery(id+"F0.wireOp",EDGE,"E26.4.3"),sQuery(id+"F0.wireOp",EDGE,"E26.4.4"),sQuery(id+"F0.wireOp",EDGE,"E26.5.0"),sQuery(id+"F0.wireOp",EDGE,"E26.5.1"),sQuery(id+"F0.wireOp",EDGE,"E26.5.2"),sQuery(id+"F0.wireOp",EDGE,"E26.5.3"),sQuery(id+"F0.wireOp",EDGE,"E26.5.4"),sQuery(id+"F0.wireOp",EDGE,"E26.6.0"),sQuery(id+"F0.wireOp",EDGE,"E26.6.1"),sQuery(id+"F0.wireOp",EDGE,"E26.6.2"),sQuery(id+"F0.wireOp",EDGE,"E26.6.3"),sQuery(id+"F0.wireOp",EDGE,"E26.6.4"),sQuery(id+"F0.wireOp",EDGE,"E26.7.0"),sQuery(id+"F0.wireOp",EDGE,"E26.7.1"),sQuery(id+"F0.wireOp",EDGE,"E26.7.2"),sQuery(id+"F0.wireOp",EDGE,"E26.7.3"),sQuery(id+"F0.wireOp",EDGE,"E26.7.4"),sQuery(id+"F0.wireOp",EDGE,"E26.8.0"),sQuery(id+"F0.wireOp",EDGE,"E26.8.1"),sQuery(id+"F0.wireOp",EDGE,"E26.8.2"),sQuery(id+"F0.wireOp",EDGE,"E26.8.3"),sQuery(id+"F0.wireOp",EDGE,"E26.8.4"),sQuery(id+"F0.wireOp",EDGE,"E26.9.0"),sQuery(id+"F0.wireOp",EDGE,"E26.9.1"),sQuery(id+"F0.wireOp",EDGE,"E26.9.2"),sQuery(id+"F0.wireOp",EDGE,"E26.9.3"),sQuery(id+"F0.wireOp",EDGE,"E26.9.4"),sQuery(id+"F0.wireOp",EDGE,"E26.10.0"),sQuery(id+"F0.wireOp",EDGE,"E26.10.1"),sQuery(id+"F0.wireOp",EDGE,"E26.10.2"),sQuery(id+"F0.wireOp",EDGE,"E26.10.3"),sQuery(id+"F0.wireOp",EDGE,"E26.10.4"),sQuery(id+"F0.wireOp",EDGE,"E26.11.0"),sQuery(id+"F0.wireOp",EDGE,"E26.11.1"),sQuery(id+"F0.wireOp",EDGE,"E26.11.2"),sQuery(id+"F0.wireOp",EDGE,"E26.11.3"),sQuery(id+"F0.wireOp",EDGE,"E26.11.4"),sQuery(id+"F0.wireOp",EDGE,"E26.12.0"),sQuery(id+"F0.wireOp",EDGE,"E26.12.1"),sQuery(id+"F0.wireOp",EDGE,"E26.12.2"),sQuery(id+"F0.wireOp",EDGE,"E26.12.3"),sQuery(id+"F0.wireOp",EDGE,"E26.12.4"),sQuery(id+"F0.wireOp",EDGE,"E26.13.0"),sQuery(id+"F0.wireOp",EDGE,"E26.13.1"),sQuery(id+"F0.wireOp",EDGE,"E26.13.2"),sQuery(id+"F0.wireOp",EDGE,"E26.13.3"),sQuery(id+"F0.wireOp",EDGE,"E26.13.4"),sQuery(id+"F0.wireOp",EDGE,"E26.14.0"),sQuery(id+"F0.wireOp",EDGE,"E26.14.1"),sQuery(id+"F0.wireOp",EDGE,"E26.14.2"),sQuery(id+"F0.wireOp",EDGE,"E26.14.3"),sQuery(id+"F0.wireOp",EDGE,"E26.14.4"),sQuery(id+"F0.wireOp",EDGE,"E26.15.0"),sQuery(id+"F0.wireOp",EDGE,"E26.15.1"),sQuery(id+"F0.wireOp",EDGE,"E26.15.2"),sQuery(id+"F0.wireOp",EDGE,"E26.15.3"),sQuery(id+"F0.wireOp",EDGE,"E26.15.4"),sQuery(id+"F0.wireOp",EDGE,"E26.16.0"),sQuery(id+"F0.wireOp",EDGE,"E26.16.1"),sQuery(id+"F0.wireOp",EDGE,"E26.16.2"),sQuery(id+"F0.wireOp",EDGE,"E26.16.3"),sQuery(id+"F0.wireOp",EDGE,"E26.16.4"),sQuery(id+"F0.wireOp",EDGE,"E26.17.0"),sQuery(id+"F0.wireOp",EDGE,"E26.17.1"),sQuery(id+"F0.wireOp",EDGE,"E26.17.2"),sQuery(id+"F0.wireOp",EDGE,"E26.17.3"),sQuery(id+"F0.wireOp",EDGE,"E26.17.4"),sQuery(id+"F0.wireOp",EDGE,"E26.18.0"),sQuery(id+"F0.wireOp",EDGE,"E26.18.1"),sQuery(id+"F0.wireOp",EDGE,"E26.18.2"),sQuery(id+"F0.wireOp",EDGE,"E26.18.3"),sQuery(id+"F0.wireOp",EDGE,"E26.18.4"),sQuery(id+"F0.wireOp",EDGE,"E26.19.0"),sQuery(id+"F0.wireOp",EDGE,"E26.19.1"),sQuery(id+"F0.wireOp",EDGE,"E26.19.2"),sQuery(id+"F0.wireOp",EDGE,"E26.19.3"),sQuery(id+"F0.wireOp",EDGE,"E26.19.4"),sQuery(id+"F0.wireOp",EDGE,"E27.trimOffspring"),sQuery(id+"F0.wireOp",EDGE,"E28.trimOffspring"),sQuery(id+"F0.wireOp",EDGE,"E29.trimOffspring"),sQuery(id+"F0.wireOp",EDGE,"E30.trimOffspring"),sQuery(id+"F0.wireOp",EDGE,"E31.trimOffspring"),sQuery(id+"F0.wireOp",EDGE,"E32.trimOffspring"),sQuery(id+"F0.wireOp",EDGE,"E33.trimOffspring"),sQuery(id+"F0.wireOp",EDGE,"E34.trimOffspring"),sQuery(id+"F0.wireOp",EDGE,"E35.trimOffspring"),sQuery(id+"F0.wireOp",EDGE,"E36.trimOffspring"),sQuery(id+"F0.wireOp",EDGE,"E37.trimOffspring"),sQuery(id+"F0.wireOp",EDGE,"E38.trimOffspring"),sQuery(id+"F0.wireOp",EDGE,"E39.trimOffspring"),sQuery(id+"F0.wireOp",EDGE,"E40.trimOffspring"),sQuery(id+"F0.wireOp",EDGE,"E41.trimOffspring"),sQuery(id+"F0.wireOp",EDGE,"E42.trimOffspring"),sQuery(id+"F0.wireOp",EDGE,"E43.trimOffspring"),sQuery(id+"F0.wireOp",EDGE,"E44.trimOffspring"),sQuery(id+"F0.wireOp",EDGE,"E45.trimOffspring")])],"isStart":true}),makeQuery(id+"F5.opExtrude","SWEPT_FACE",FACE,{"disambiguationData":[OSD([sQuery(id+"F4.wireOp",EDGE,"E55")])]})]});
            chamfer(context, id + "F7", {"entities" : qUnion([Q0]), "width" : 2 * mm, "tangentPropagation" : true});
        }
    });
